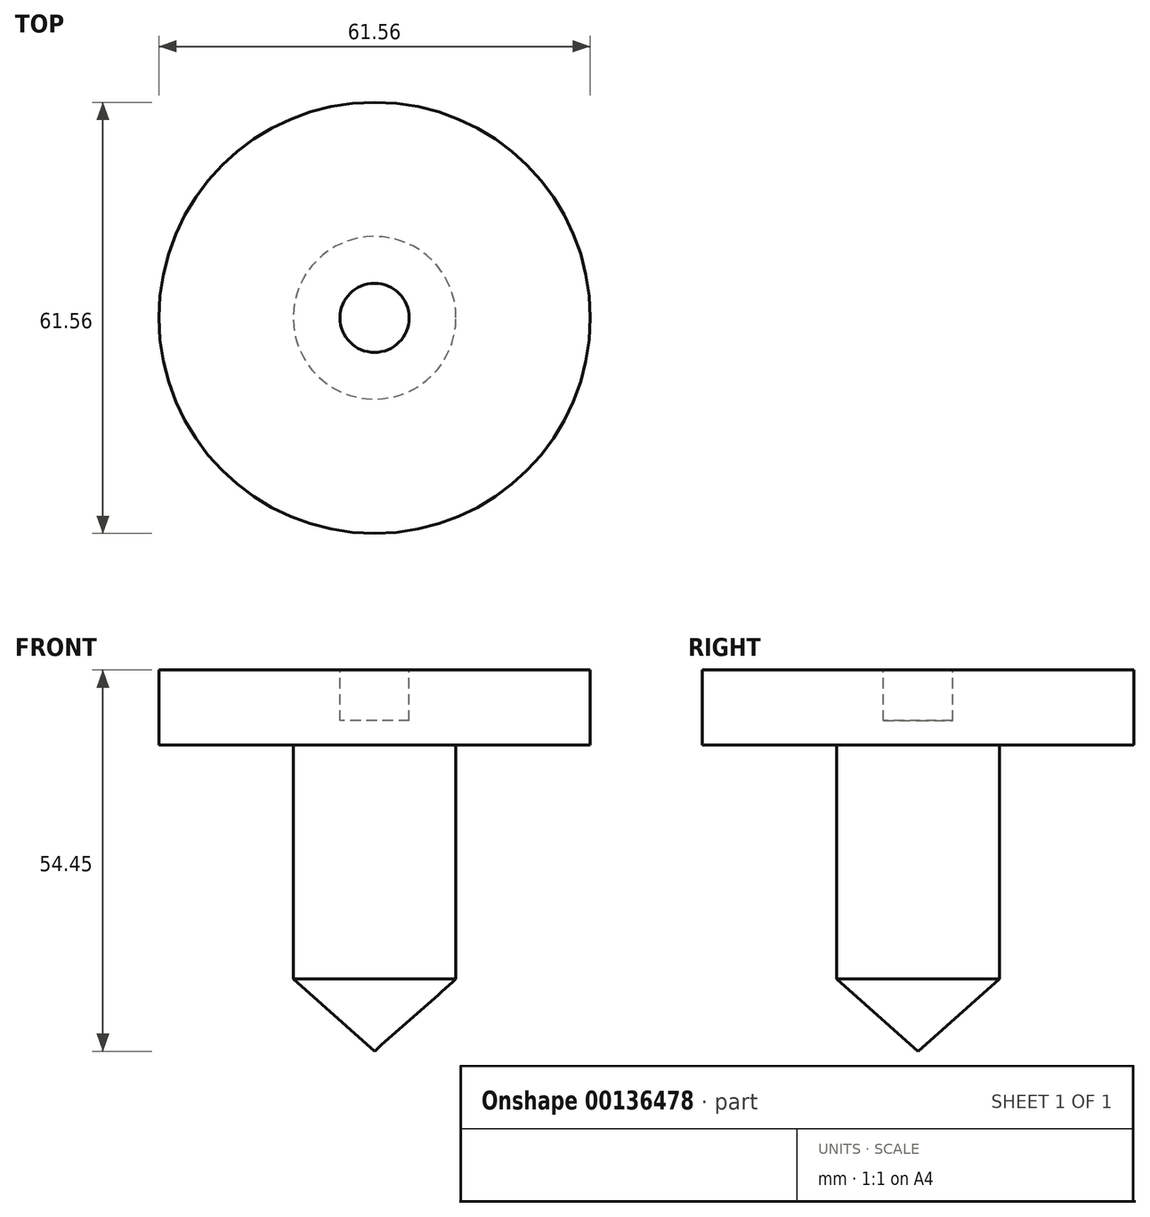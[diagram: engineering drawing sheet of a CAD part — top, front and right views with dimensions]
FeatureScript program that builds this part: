
annotation { "Feature Type Name" : "Feature", "Feature Type Description" : "" }
export const myFeature = defineFeature(function(context is Context, id is Id, definition is map)
    precondition{}
    {
        {
            var Q0;
            Q0=qCreatedBy(makeId("Front.planeOp"),FACE);
            var sketch = newSketch(context, id + "F0", { "sketchPlane" : qUnion([Q0])});
            skLineSegment(sketch, "E0", {"start": v(0, 0) * mm, "end": v(11.62, 10.3) * mm});
            skLineSegment(sketch, "E1", {"start": v(11.62, 10.3) * mm, "end": v(11.62, 43.7) * mm});
            skLineSegment(sketch, "E2", {"start": v(11.62, 43.7) * mm, "end": v(30.78, 43.7) * mm});
            skLineSegment(sketch, "E3", {"start": v(30.78, 43.7) * mm, "end": v(30.78, 54.45) * mm});
            skLineSegment(sketch, "E4", {"start": v(30.78, 54.45) * mm, "end": v(4.94, 54.45) * mm});
            skLineSegment(sketch, "E5", {"start": v(4.94, 54.45) * mm, "end": v(4.94, 47.2) * mm});
            skLineSegment(sketch, "E6", {"start": v(4.94, 47.2) * mm, "end": v(0, 47.2) * mm});
            skLineSegment(sketch, "E7", {"start": v(0, 47.2) * mm, "end": v(0, 0) * mm});
            skSolve(sketch);
        }
        {
            var Q0;
            Q0=makeQuery(id+"F0.imprint","IMPRINT",FACE,{"disambiguationData":[TD([[makeQuery(id+"F0.imprint","IMPRINT",EDGE,{"derivedFrom":sQuery(id+"F0.wireOp",EDGE,"E0")}),1.0]])]});
            var Q1;
            Q1=sQuery(id+"F0.wireOp",EDGE,"E7");
            revolve(context, id + "F1", {"entities" : qUnion([Q0]), "axis" : qUnion([Q1]), "revolveType" : RevolveType.FULL});
        }
    });
